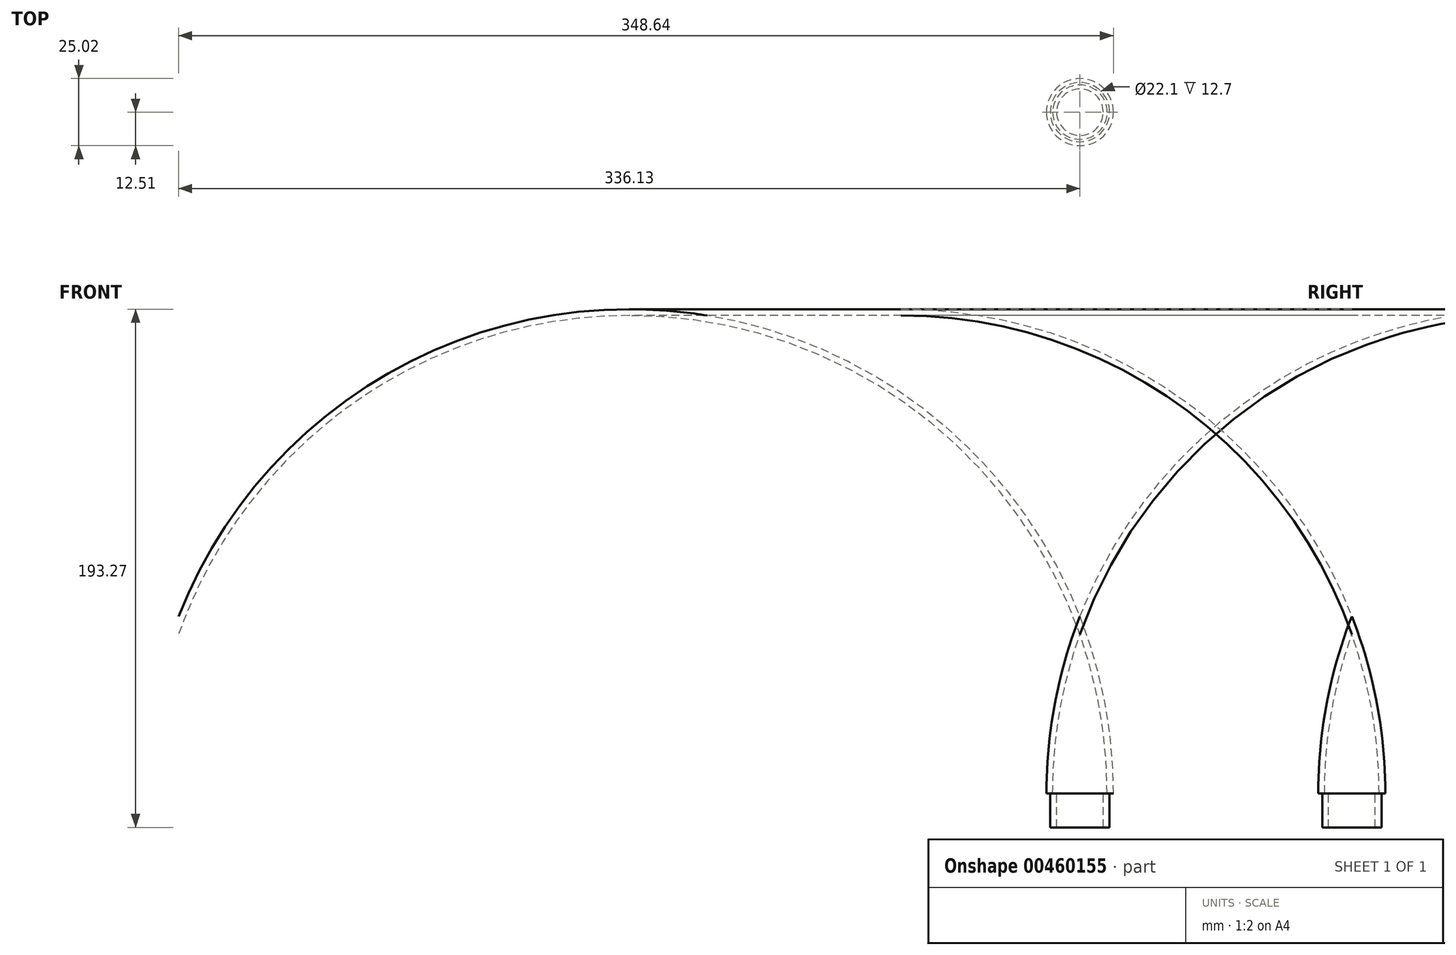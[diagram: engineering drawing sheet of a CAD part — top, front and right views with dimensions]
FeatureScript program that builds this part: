
annotation { "Feature Type Name" : "Feature", "Feature Type Description" : "" }
export const myFeature = defineFeature(function(context is Context, id is Id, definition is map)
    precondition{}
    {
        {
            var Q0;
            Q0=qCreatedBy(makeId("Front.planeOp"),FACE);
            var sketch = newSketch(context, id + "F0", { "sketchPlane" : qUnion([Q0])});
            skArc(sketch, "E0", {"start": v(0, 66.04) * mm, "mid": v(-9.35, 33.6) * mm, "end": v(-12.5, 0) * mm});
            skArc(sketch, "E1", {"start": v(0, 59.28) * mm, "mid": v(-7.6, 30.07) * mm, "end": v(-10.15, 0) * mm});
            skLineSegment(sketch, "E2", {"start": v(0, 59.28) * mm, "end": v(0, 66.04) * mm});
            skLineSegment(sketch, "E3", {"start": v(-12.5, 0) * mm, "end": v(-10.15, 0) * mm});
            skSolve(sketch);
        }
        {
            var Q0;
            Q0 = qSketchRegion(id + "F0", true);
            var Q1;
            Q1=sQuery(id+"F0.wireOp",EDGE,"E2");
            revolve(context, id + "F1", {"entities" : qUnion([Q0]), "axis" : qUnion([Q1]), "revolveType" : RevolveType.FULL});
        }
        {
            var Q0;
            Q0=qCreatedBy(makeId("Top.planeOp"),FACE);
            var sketch = newSketch(context, id + "F2", { "sketchPlane" : qUnion([Q0])});
            skCircle(sketch, "E4", {"center": v(0, 0) * mm, "radius": 11.05 * mm});
            skCircle(sketch, "E5", {"center": v(0, 0) * mm, "radius": 8.69 * mm});
            skSolve(sketch);
        }
        {
            var Q0;
            Q0=makeQuery(id+"F2.imprint","IMPRINT",FACE,{"disambiguationData":[TD([[makeQuery(id+"F2.imprint","IMPRINT",EDGE,{"derivedFrom":sQuery(id+"F2.wireOp",EDGE,"E4")}),1.0]])]});
            extrude(context, id + "F3", {"entities" : qUnion([Q0]), "operationType" : NewBodyOperationType.ADD, "oppositeDirection" : true, "depth" : 12.7 * mm});
        }
        {
            var Q0;
            Q0=qCreatedBy(makeId("Front.planeOp"),FACE);
            var sketch = newSketch(context, id + "F4", { "sketchPlane" : qUnion([Q0])});
            skArc(sketch, "E6", {"start": v(0, 59.28) * mm, "mid": v(-7.6, 30.07) * mm, "end": v(-10.15, 0) * mm});
            skLineSegment(sketch, "E7", {"start": v(-10.15, 0) * mm, "end": v(0, 0) * mm});
            skArc(sketch, "E8.MirrorCS", {"start": v(0, 59.28) * mm, "mid": v(7.6, 30.07) * mm, "end": v(10.15, 0) * mm});
            skLineSegment(sketch, "E9.MirrorCS", {"start": v(10.15, 0) * mm, "end": v(0, 0) * mm});
            skSolve(sketch);
        }
        {
            var Q0;
            Q0 = qConstructionFilter(qBodyType(qCreatedBy(id + "F4" ,EDGE), BodyType.WIRE), ConstructionObject.NO);
            extrude(context, id + "F5", {"bodyType" : ExtendedToolBodyType.SURFACE, "surfaceEntities" : qUnion([Q0]), "depth" : 6.35 * mm, "symmetric" : true});
        }
        {
            var Q0;
            Q0=qCreatedBy(makeId("Front.planeOp"),FACE);
            var sketch = newSketch(context, id + "F6", { "sketchPlane" : qUnion([Q0])});
            skArc(sketch, "E10", {"start": v(0, 48.91) * mm, "mid": v(-5.22, 24.7) * mm, "end": v(-6.97, 0) * mm});
            skLineSegment(sketch, "E11", {"start": v(-6.97, 0) * mm, "end": v(0, 0) * mm});
            skArc(sketch, "E12.MirrorCS", {"start": v(0, 48.91) * mm, "mid": v(5.22, 24.7) * mm, "end": v(6.97, 0) * mm});
            skLineSegment(sketch, "E13.MirrorCS", {"start": v(6.97, 0) * mm, "end": v(0, 0) * mm});
            skSolve(sketch);
        }
        {
            var Q0;
            Q0 = qSketchRegion(id + "F6", true);
            extrude(context, id + "F7", {"entities" : qUnion([Q0]), "operationType" : NewBodyOperationType.REMOVE, "depth" : 6.6 * mm, "symmetric" : true});
        }
    });
